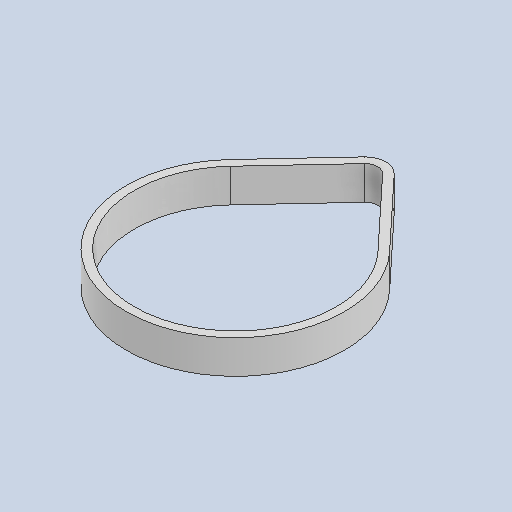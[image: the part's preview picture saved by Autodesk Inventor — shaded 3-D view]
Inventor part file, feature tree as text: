
AUTODESK INVENTOR PART (.ipt)
format: ipt  version: 2022.3 (Build 263350000, 350)  size: 87,552 bytes
history: native  units: in
note: dims shown in document units (in); Inventor stores cm internally (conversion verified against a paired STEP export)
features: extrude x1
ambient origin geometry x8: Origin, YZ Plane, XZ Plane, XY Plane, X Axis, Y Axis, Z Axis, Center Point
bodies: Solid1 (feature_tree)
feature tree (1):
  extrude  "Extrude-Thin1"  [1 undecoded]
note: 1 required parameter value undecoded (feature->parameter linkage not recoverable at this tier; creation-order binding heuristic only, values carry confidence <= 0.55)
